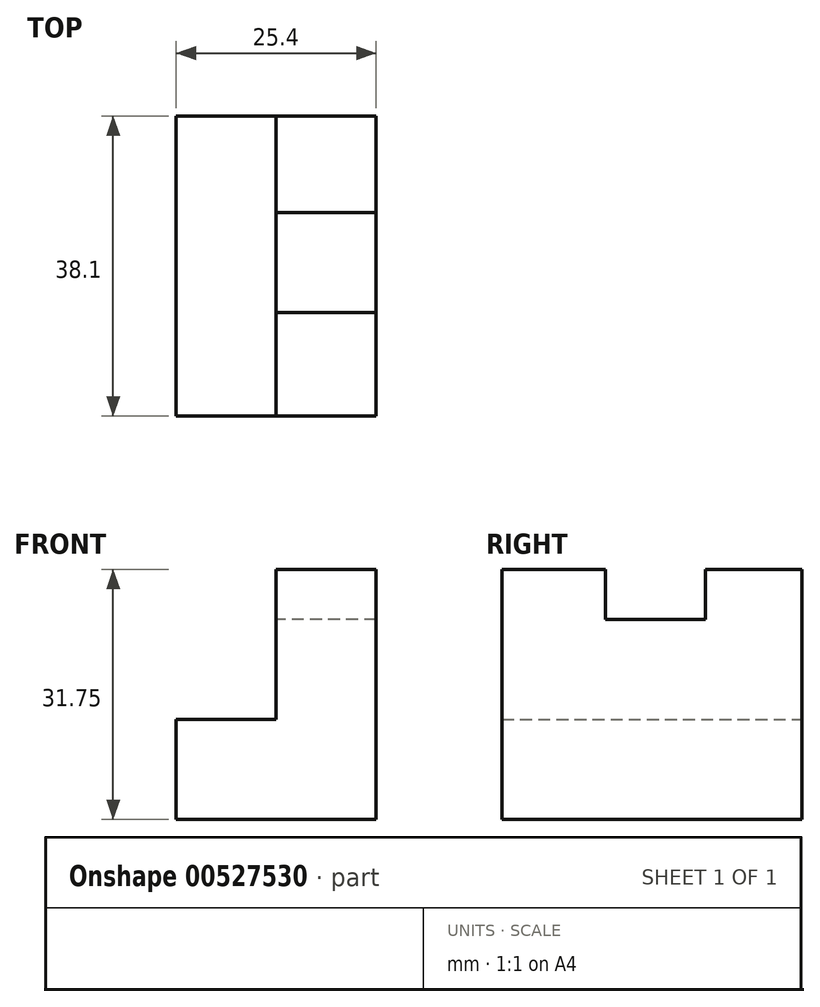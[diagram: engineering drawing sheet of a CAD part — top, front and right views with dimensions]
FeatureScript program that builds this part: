
annotation { "Feature Type Name" : "Feature", "Feature Type Description" : "" }
export const myFeature = defineFeature(function(context is Context, id is Id, definition is map)
    precondition{}
    {
        {
            var Q0;
            Q0=qCreatedBy(makeId("Front.planeOp"),FACE);
            var sketch = newSketch(context, id + "F0", { "sketchPlane" : qUnion([Q0])});
            skLineSegment(sketch, "E0", {"start": v(0, 0) * mm, "end": v(0, 12.7) * mm});
            skLineSegment(sketch, "E1", {"start": v(0, 0) * mm, "end": v(25.4, 0) * mm});
            skLineSegment(sketch, "E2", {"start": v(25.4, 0) * mm, "end": v(25.4, 31.75) * mm});
            skLineSegment(sketch, "E3", {"start": v(25.4, 31.75) * mm, "end": v(12.7, 31.75) * mm});
            skLineSegment(sketch, "E4", {"start": v(12.7, 31.75) * mm, "end": v(12.7, 12.7) * mm});
            skLineSegment(sketch, "E5", {"start": v(12.7, 12.7) * mm, "end": v(0, 12.7) * mm});
            skSolve(sketch);
        }
        {
            var Q0;
            Q0 = qSketchRegion(id + "F0", true);
            extrude(context, id + "F1", {"entities" : qUnion([Q0]), "depth" : 38.1 * mm, "offsetDistance" : 25.4 * mm});
        }
        {
            var Q0;
            Q0=makeQuery(id+"F1.opExtrude","SWEPT_FACE",FACE,{"disambiguationData":[OSD([sQuery(id+"F0.wireOp",EDGE,"E4")])]});
            var sketch = newSketch(context, id + "F2", { "sketchPlane" : qUnion([Q0])});
            skLineSegment(sketch, "E6", {"start": v(12.27, 31.75) * mm, "end": v(12.27, 25.4) * mm});
            skLineSegment(sketch, "E7", {"start": v(12.27, 25.4) * mm, "end": v(24.97, 25.4) * mm});
            skLineSegment(sketch, "E8", {"start": v(24.97, 25.4) * mm, "end": v(24.97, 31.75) * mm});
            skSolve(sketch);
        }
        {
            var Q0;
            Q0 = qSketchRegion(id + "F2", true);
            var Q1;
            {var subQ0=sQuery(id+"F2.wireOp",EDGE,"E6");Q1=makeQuery(id+"F2.imprint","IMPRINT",FACE,{"disambiguationData":[TD([[makeQuery(id+"F2.imprint","IMPRINT",EDGE,{"derivedFrom":subQ0}),1.0]])]});}
            extrude(context, id + "F3", {"entities" : qUnion([Q0, Q1]), "operationType" : NewBodyOperationType.REMOVE, "oppositeDirection" : true, "depth" : 12.7 * mm, "offsetDistance" : 25.4 * mm});
        }
    });
